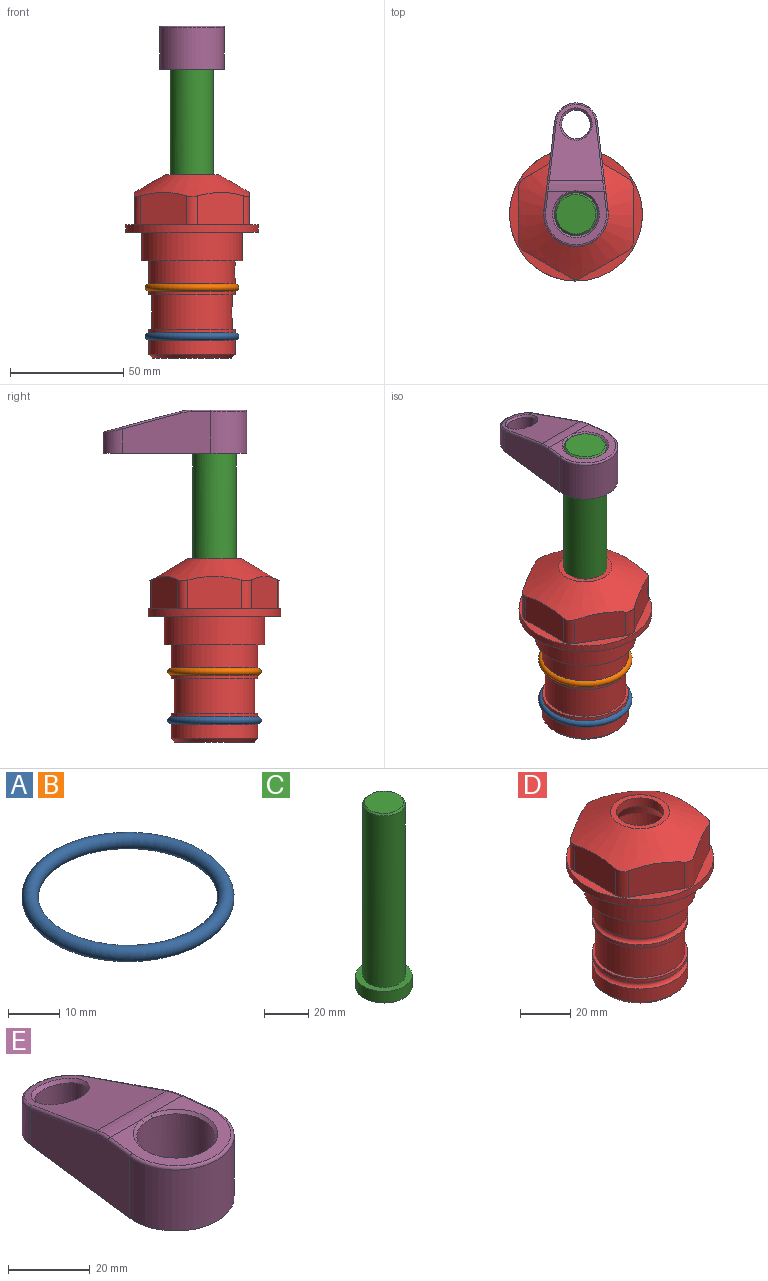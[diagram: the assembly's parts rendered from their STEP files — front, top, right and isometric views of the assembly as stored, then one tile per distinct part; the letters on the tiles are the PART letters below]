
ASSEMBLY  parts=5 mates=4
PART A: 1 faces, bbox 44.7x44.7x3.2 mm
  f0: torus R=19.05mm, axis (0,0,1), area 1193.9mm2
PART B: same geometry as A
PART C: 6 faces, bbox 25.4x25.4x101.6 mm
  f0: plane 17.46x17.46mm, normal (0,0,1), area 239.5mm2, adj f5
  f1: plane 25.4x25.4mm, normal (0,0,-1), area 506.7mm2, adj f2
  f2: cylinder r=12.7mm len=25.4mm, axis (0,0,1), area 506.7mm2, adj f1,f3
  f3: plane 25.4x25.4mm, normal (0,0,1), area 221.7mm2, adj f2,f4
  f4: cylinder r=9.53mm len=94.46mm, axis (0,0,1), area 5653mm2, adj f3,f5
  f5: cone r=8.73mm half-angle=45deg, axis (0,0,-1), area 64.4mm2, adj f0,f4
PART D: 36 faces, bbox 58.7x58.7x81 mm
  f0: cylinder r=17.78mm len=35.56mm, axis (0,0,1), area 1670.8mm2, adj f23,f24,f31
  f1: cylinder r=19.05mm len=38.1mm, axis (0,0,1), area 1191.9mm2, adj f26,f27,f30
  f2: plane 58.66x58.66mm, normal (0,0,-1), area 1150.6mm2, adj f3,f28
  f3: cylinder r=29.33mm len=58.66mm, axis (0,0,-1), area 585.1mm2, adj f2,f4
  f4: plane 58.66x58.66mm, normal (0,0,1), area 475.9mm2, adj f3,f5,f6,f7,f8,f9,f10,f11
  f5: plane 20.32x14.34mm, normal (-0.5,0.87,0), area 324.4mm2, adj f4,f15,f16,f17
  f6: plane 20.32x14.34mm, normal (0.5,0.87,0), area 324.4mm2, adj f4,f14,f15,f17
  f7: plane 23.48x14.34mm, normal (1,0,0), area 324.4mm2, adj f4,f13,f14,f17
  f8: plane 20.32x14.34mm, normal (0.5,-0.87,0), area 324.4mm2, adj f4,f12,f13,f17
  f9: plane 20.32x14.34mm, normal (-0.5,-0.87,0), area 324.4mm2, adj f4,f11,f12,f17
  f10: plane 23.48x14.34mm, normal (-1,0,0), area 324.4mm2, adj f4,f11,f16,f17
  f11: cylinder r=5.08mm len=12.85mm, axis (0,0,-1), area 67.2mm2, adj f4,f9,f10,f17
  f12: cylinder r=5.08mm len=12.85mm, axis (0,0,-1), area 67.2mm2, adj f4,f8,f9,f17
  f13: cylinder r=5.08mm len=12.85mm, axis (0,0,-1), area 67.2mm2, adj f4,f7,f8,f17
  f14: cylinder r=5.08mm len=12.85mm, axis (0,0,-1), area 67.2mm2, adj f4,f6,f7,f17
  f15: cylinder r=5.08mm len=12.85mm, axis (0,0,-1), area 67.2mm2, adj f4,f5,f6,f17
  f16: cylinder r=5.08mm len=12.85mm, axis (0,0,-1), area 67.2mm2, adj f4,f5,f10,f17
  f17: cone r=11.73mm half-angle=60deg, axis (0,0,-1), area 2071.8mm2, adj f5,f6,f7,f8,f9,f10,f11,f12
  f18: plane 23.46x23.46mm, normal (0,0,1), area 147.4mm2, adj f17,f35
  f19: plane 34.93x34.93mm, normal (0,0,-1), area 958mm2, adj f29
  f20: cylinder r=19.05mm len=38.1mm, axis (0,0,1), area 760.1mm2, adj f21,f29
  f21: torus R=19.05mm, axis (0,0,1), area 565.3mm2, adj f20,f22
  f22: cylinder r=19.05mm len=38.1mm, axis (0,0,1), area 190mm2, adj f21,f23
  f23: plane 38.1x38.1mm, normal (0,0,1), area 146.9mm2, adj f0,f22
  f24: plane 38.1x38.1mm, normal (0,0,-1), area 146.9mm2, adj f0,f25
  f25: cylinder r=19.05mm len=38.1mm, axis (0,0,1), area 190mm2, adj f24,f26
  f26: torus R=19.05mm, axis (0,0,1), area 565.3mm2, adj f1,f25
  f27: plane 44.45x44.45mm, normal (0,0,-1), area 411.7mm2, adj f1,f28
  f28: cylinder r=22.23mm len=44.45mm, axis (0,0,1), area 1773.5mm2, adj f2,f27
  f29: cone r=19.05mm half-angle=45deg, axis (0,0,1), area 257.5mm2, adj f19,f20
  f30: cylinder r=3.17mm len=6.75mm, axis (-1,0,0), area 128mm2, adj f1,f33
  f31: cylinder r=3.17mm len=6.35mm, axis (-1,0,0), area 102.5mm2, adj f0,f33
  f32: plane 25.4x25.4mm, normal (0,0,1), area 506.7mm2, adj f33
  f33: cylinder r=12.7mm len=66.42mm, axis (0,0,-1), area 5236.2mm2, adj f30,f31,f32,f34
  f34: cone r=9.53mm half-angle=30deg, axis (0,0,-1), area 443.4mm2, adj f33,f35
  f35: cylinder r=9.53mm len=19.05mm, axis (0,0,-1), area 240.9mm2, adj f18,f34
PART E: 31 faces, bbox 31.7x65.5x19.8 mm
  f0: plane 39.12x18.26mm, normal (0.99,0.12,0), area 612.2mm2, adj f1,f4,f7,f11,f13,f15
  f1: cylinder r=9.53mm len=18.91mm, axis (0,0,-1), area 296.1mm2, adj f0,f2,f7,f17
  f2: plane 39.12x18.26mm, normal (-0.99,0.12,0), area 612.2mm2, adj f1,f4,f7,f12,f14,f16
  f3: cylinder r=6.35mm len=12.7mm, axis (0,0,-1), area 362.4mm2, adj f7,f18
  f4: cylinder r=14.29mm len=28.58mm, axis (0,0,-1), area 882.2mm2, adj f0,f2,f7,f10
  f5: cylinder r=9.53mm len=19.05mm, axis (0,0,-1), area 1092.6mm2, adj f7,f19,f20
  f6: plane 26.99x23.69mm, normal (0,0,1), area 216.2mm2, adj f9,f10,f11,f12,f19
  f7: plane 63.5x28.58mm, normal (0,0,-1), area 661.8mm2, adj f0,f1,f2,f3,f4,f5,f22,f23
  f8: plane 33.52x23.6mm, normal (0,0.26,0.97), area 486mm2, adj f9,f15,f16,f17,f18
  f9: cylinder r=19.05mm len=24.72mm, axis (1,0,0), area 120.4mm2, adj f6,f8,f13,f14,f20
  f10: torus R=13.49mm, axis (0,0,1), area 59mm2, adj f4,f6,f11,f12
  f11: cylinder r=0.79mm len=8.67mm, axis (0.12,-0.99,0), area 10.8mm2, adj f0,f6,f10,f13
  f12: cylinder r=0.79mm len=8.67mm, axis (0.12,0.99,0), area 10.8mm2, adj f2,f6,f10,f14
  f13: bspline ~4.95x1.42mm, area 6.1mm2, adj f0,f9,f11,f15
  f14: bspline ~4.95x1.42mm, area 6.1mm2, adj f2,f9,f12,f16
  f15: cylinder r=0.79mm len=25.95mm, axis (0.12,-0.96,0.26), area 32.9mm2, adj f0,f8,f13,f17
  f16: cylinder r=0.79mm len=25.95mm, axis (0.12,0.96,-0.26), area 32.9mm2, adj f2,f8,f14,f17
  f17: bspline ~18.91x8.38mm, area 30mm2, adj f1,f8,f15,f16
  f18: bspline ~14.29x14.29mm, area 48.3mm2, adj f3,f8
  f19: cone r=9.53mm half-angle=45deg, axis (0,0,1), area 66.5mm2, adj f5,f6,f20
  f20: bspline ~3.22x0.96mm, area 3.5mm2, adj f5,f9,f19
  f21: plane 2.75x2.72mm, normal (0,0,-1), area 2.9mm2, adj f23,f25,f28
  f22: plane 23.05x15.88mm, normal (-0.99,-0.12,0), area 323.6mm2, adj f7,f25,f26,f27,f28,f29
  f23: plane 23.05x15.88mm, normal (0.99,-0.12,0), area 323.6mm2, adj f7,f21,f25,f27,f28,f30
  f24: cylinder r=9.53mm len=10.69mm, axis (0,0,-1), area 114.7mm2, adj f7,f27,f29,f30
  f25: cylinder r=12.7mm len=20.59mm, axis (0,0,-1), area 381.1mm2, adj f7,f21,f22,f23,f26,f28
  f26: plane 2.75x2.72mm, normal (0,0,-1), area 2.9mm2, adj f22,f25,f28
  f27: plane 19.72x18.37mm, normal (0,-0.26,-0.97), area 291.8mm2, adj f22,f23,f24,f28,f29,f30
  f28: cylinder r=15.88mm len=19.92mm, axis (1,0,0), area 54.8mm2, adj f21,f22,f23,f25,f26,f27
  f29: cylinder r=1.59mm len=11mm, axis (0,0,-1), area 34.7mm2, adj f7,f22,f24,f27
  f30: cylinder r=1.59mm len=11mm, axis (0,0,-1), area 34.7mm2, adj f7,f23,f24,f27
PLACE A t=(0,0,-21.59)mm
PLACE B at identity
PLACE C t=(0,0,27.55)mm
PLACE D at identity fixed
PLACE E t=(0,0,27.55)mm
MATE fastened E.f4 <-> C.f2  axis (0,0,1) through (0,0,91.05)mm
MATE fastened A.f0 <-> D.f0  axis (0,0,1) through (0,0,-46.1)mm
MATE fastened B.f0 <-> D.f0  axis (0,0,1) through (0,0,-24.51)mm
MATE slider C.f2 <-> D.f0  axis (0,0,-1) through (0,0,-10.55)mm
